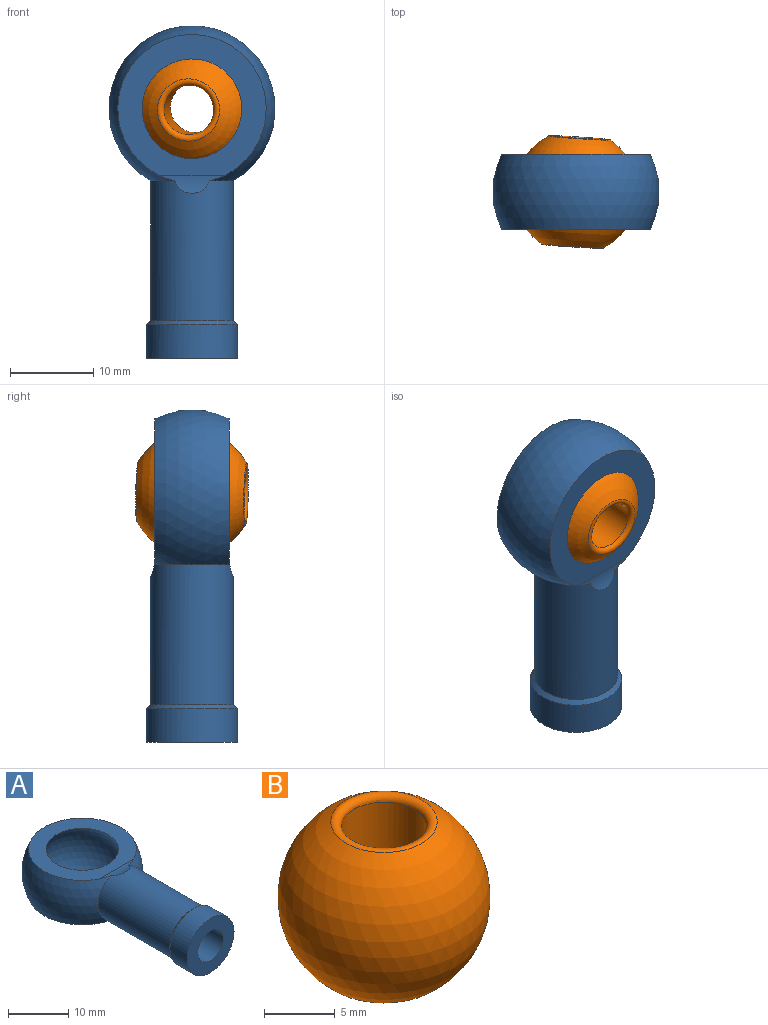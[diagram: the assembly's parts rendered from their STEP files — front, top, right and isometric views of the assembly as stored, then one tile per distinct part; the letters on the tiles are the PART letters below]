
ASSEMBLY  parts=2 mates=1
PART A: 12 faces, bbox 20x40x11 mm
  f0: cylinder r=5mm len=16.84mm, axis (0,-1,0), area 519.5mm2, adj f1,f4,f5,f8
  f1: sphere r=10mm, area 484.9mm2, adj f0,f2,f3,f4,f5
  f2: plane 17.86x16.92mm, normal (0,0,-1), area 132.3mm2, adj f1,f4,f11
  f3: plane 17.86x16.92mm, normal (0,0,1), area 132.3mm2, adj f1,f5,f11
  f4: cylinder r=5mm len=8mm, axis (-1,0,0), area 9.1mm2, adj f0,f1,f2
  f5: cylinder r=5mm len=8mm, axis (-1,0,0), area 9.1mm2, adj f0,f1,f3
  f6: cylinder r=5.5mm len=11mm, axis (0,-1,0), area 138.2mm2, adj f7,f8
  f7: plane 11x11mm, normal (0,-1,0), area 66.8mm2, adj f6,f9
  f8: cone r=5mm half-angle=45deg, axis (0,-1,0), area 23.3mm2, adj f0,f6
  f9: cylinder r=3mm len=14.1mm, axis (0,-1,0), area 265.8mm2, adj f7,f10
  f10: plane 6x6mm, normal (0,-1,0), area 28.3mm2, adj f9
  f11: sphere r=7.5mm, area 424.1mm2, adj f2,f3
PART B: 4 faces, bbox 15x15x13.1 mm
  f0: sphere r=7.5mm, area 612.2mm2, adj f2,f3
  f1: cylinder r=3mm len=12.12mm, axis (0,0,-1), area 228.5mm2, adj f2,f3
  f2: torus R=3.5mm, axis (0,0,1), area 21.7mm2, adj f0,f1
  f3: torus R=3.5mm, axis (0,0,-1), area 21.7mm2, adj f0,f1
PLACE A rot(axis=(1,0,0),90deg) t=(0,0,15)mm
PLACE B rot(axis=(0.92,-0.31,0.24),95deg) t=(8.3,-0.25,17.51)mm
MATE ball B.f1 <-> A.f1  axis (-0.06,-1,-0.02) through (0,0,30)mm
